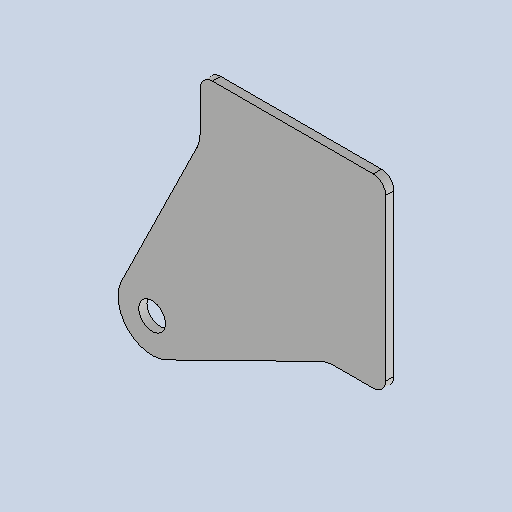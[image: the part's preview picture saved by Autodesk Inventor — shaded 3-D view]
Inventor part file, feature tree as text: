
AUTODESK INVENTOR PART (.ipt)
format: ipt  version: 2025 (Build 290162010, 162A)  size: 151,552 bytes
history: native  units: mm
features: other x2, sheet_metal_op x1, chamfer x1, sketch x1
ambient origin geometry x8: Origin, YZ Plane, XZ Plane, XY Plane, X Axis, Y Axis, Z Axis, Center Point
bodies: Solid1 (feature_tree)
feature tree (5):
  sheet_metal_op  "Face1"
  chamfer  "Corner Round3"
  sketch  "Sketch1"  dims[d2=80.0mm d3=80.0mm d6=4.0mm d29=5.0mm d30=13.0mm d31=10.0mm d32=40.0mm d34=5.0mm d35=15.0mm d36=25.0mm d37=6.0mm]
  other  "Plate1"
  other  "Definition1"
